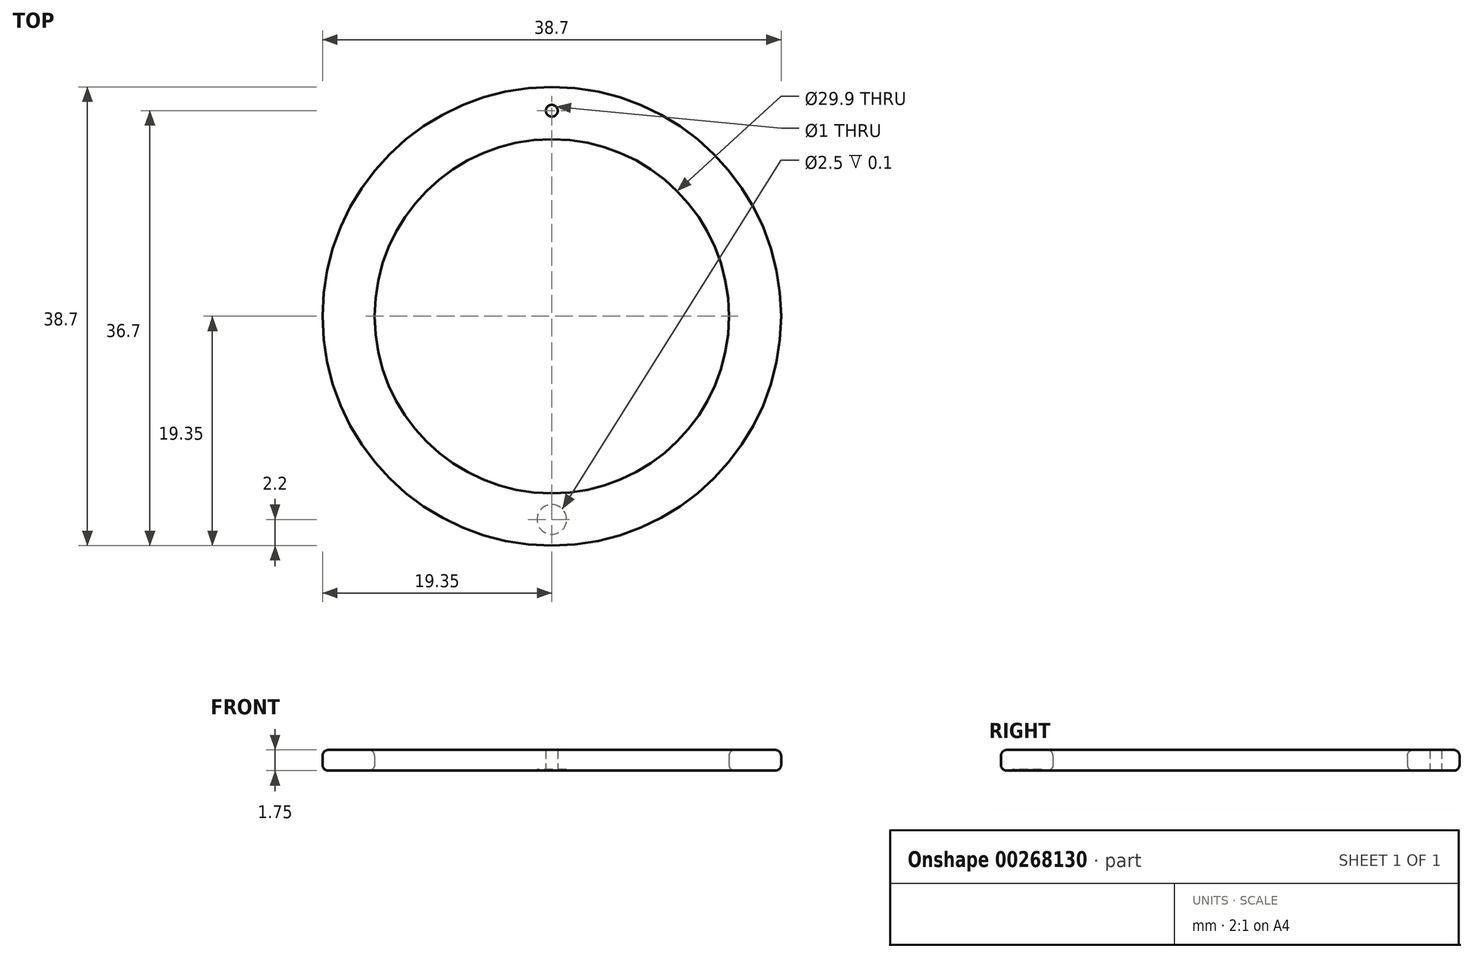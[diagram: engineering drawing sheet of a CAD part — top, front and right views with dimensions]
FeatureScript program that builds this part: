
annotation { "Feature Type Name" : "Feature", "Feature Type Description" : "" }
export const myFeature = defineFeature(function(context is Context, id is Id, definition is map)
    precondition{}
    {
        {
            var Q0;
            Q0=qCreatedBy(makeId("Top.planeOp"),FACE);
            var sketch = newSketch(context, id + "F0", { "sketchPlane" : qUnion([Q0])});
            skCircle(sketch, "E0", {"center": v(0, 0) * mm, "radius": 19.35 * mm});
            skCircle(sketch, "E1", {"center": v(0, 0) * mm, "radius": 14.95 * mm});
            skCircle(sketch, "E2", {"center": v(0, -17.15) * mm, "radius": 1.25 * mm});
            skLineSegment(sketch, "E3", {"start": v(0, 19.35) * mm, "end": v(0, 17.35) * mm});
            skCircle(sketch, "E4", {"center": v(0, 17.35) * mm, "radius": 0.5 * mm});
            skSolve(sketch);
        }
        {
            var Q0;
            Q0=makeQuery(id+"F0.imprint","IMPRINT",FACE,{"disambiguationData":[TD([[makeQuery(id+"F0.imprint","IMPRINT",EDGE,{"derivedFrom":sQuery(id+"F0.wireOp",EDGE,"E0")}),1.0]])]});
            var Q1;
            Q1=makeQuery(id+"F0.imprint","IMPRINT",FACE,{"disambiguationData":[TD([[makeQuery(id+"F0.imprint","IMPRINT",EDGE,{"derivedFrom":sQuery(id+"F0.wireOp",EDGE,"E2")}),1.0]])]});
            extrude(context, id + "F1", {"entities" : qUnion([Q0, Q1]), "depth" : 1.75 * mm, "offsetDistance" : 25 * mm});
        }
        {
            var Q0;
            Q0=makeQuery(id+"F1.opExtrude","CAP_EDGE",EDGE,{"disambiguationData":[OSD([sQuery(id+"F0.wireOp",EDGE,"E0")])],"isStart":false});
            var Q1;
            Q1=makeQuery(id+"F1.opExtrude","CAP_EDGE",EDGE,{"disambiguationData":[OSD([sQuery(id+"F0.wireOp",EDGE,"E1")])],"isStart":false});
            var Q2;
            Q2=makeQuery(id+"F1.opExtrude","CAP_EDGE",EDGE,{"disambiguationData":[OSD([sQuery(id+"F0.wireOp",EDGE,"E0")])],"isStart":true});
            var Q3;
            Q3=makeQuery(id+"F1.opExtrude","CAP_EDGE",EDGE,{"disambiguationData":[OSD([sQuery(id+"F0.wireOp",EDGE,"E1")])],"isStart":true});
            fillet(context, id + "F2", {"entities" : qUnion([Q0, Q1, Q2, Q3]), "radius" : 0.5 * mm, "tangentPropagation" : true, "allowEdgeOverflow" : false});
        }
        {
            var Q0;
            Q0=makeQuery(id+"F0.imprint","IMPRINT",FACE,{"disambiguationData":[TD([[makeQuery(id+"F0.imprint","IMPRINT",EDGE,{"derivedFrom":sQuery(id+"F0.wireOp",EDGE,"E2")}),1.0]])]});
            extrude(context, id + "F3", {"entities" : qUnion([Q0]), "operationType" : NewBodyOperationType.REMOVE, "depth" : 0.1 * mm, "offsetDistance" : 25 * mm});
        }
    });
